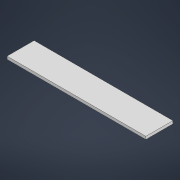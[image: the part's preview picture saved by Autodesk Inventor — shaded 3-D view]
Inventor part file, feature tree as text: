
AUTODESK INVENTOR PART (.ipt)
format: ipt  version: 2022 (Build 260153000, 153)  size: 86,528 bytes
history: native  units: mm
features: other x1, extrude x1, sketch x1
ambient origin geometry x8: Origin, YZ Plane, XZ Plane, XY Plane, X Axis, Y Axis, Z Axis, Center Point
bodies: Body1 (feature_tree)
feature tree (3):
  other  "Твердое тело1"
  extrude  "Выдавливание1"  Depth=600.0mm
  sketch  "Эскиз1"
